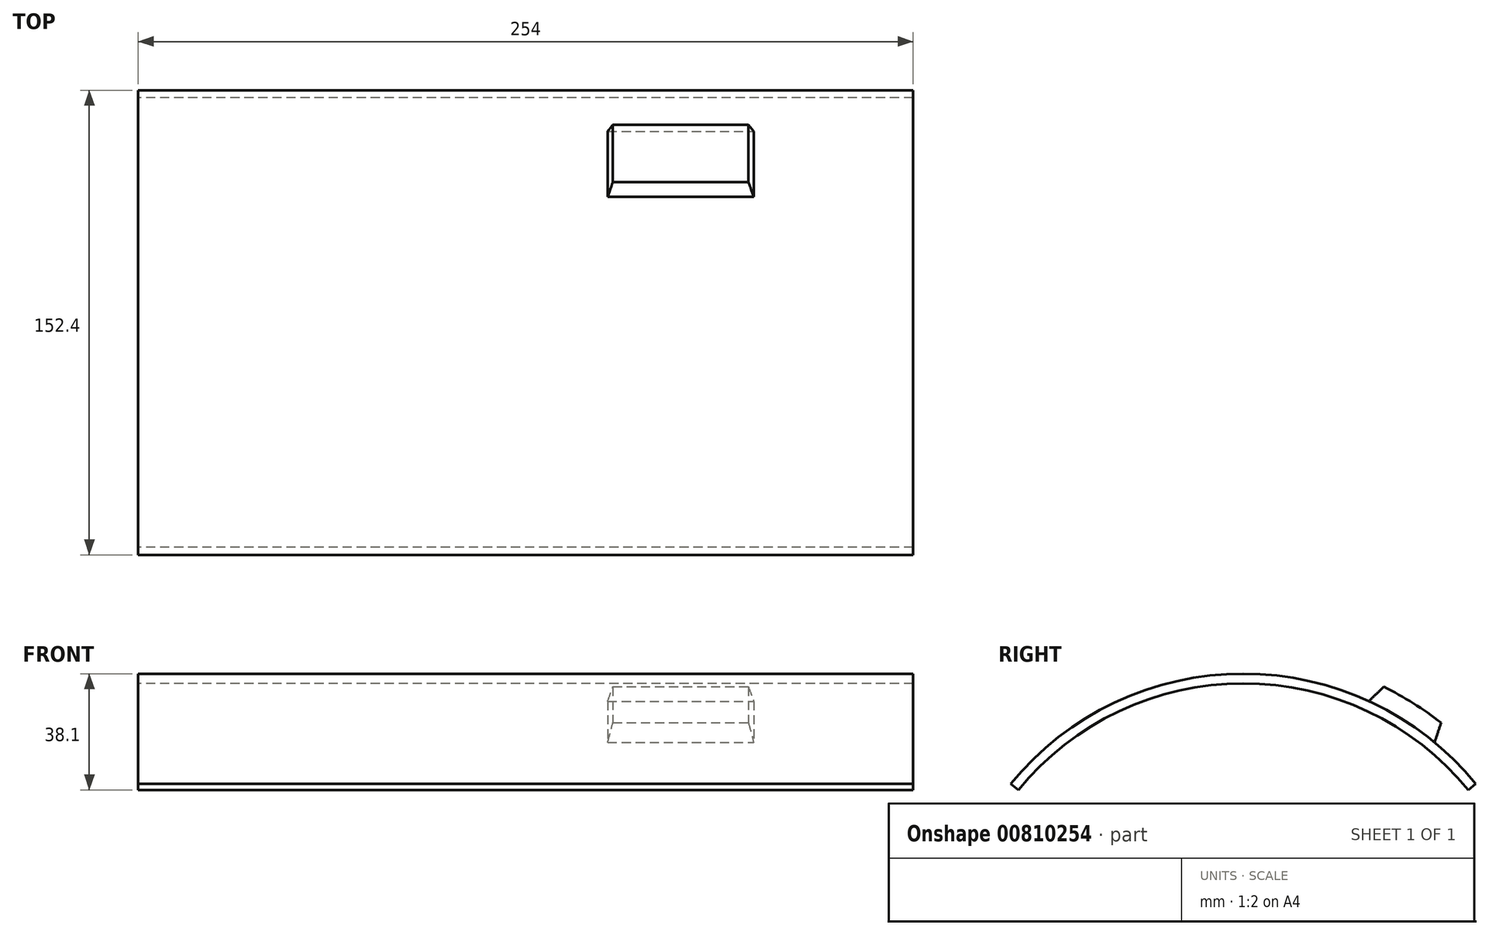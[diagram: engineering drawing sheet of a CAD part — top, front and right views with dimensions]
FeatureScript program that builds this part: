
annotation { "Feature Type Name" : "Feature", "Feature Type Description" : "" }
export const myFeature = defineFeature(function(context is Context, id is Id, definition is map)
    precondition{}
    {
        {
            var Q0;
            Q0=qCreatedBy(makeId("Right.planeOp"),FACE);
            var sketch = newSketch(context, id + "F0", { "sketchPlane" : qUnion([Q0])});
            skLineSegment(sketch, "E0", {"start": v(0, 0) * mm, "end": v(0, 53) * mm, "construction": true});
            skArc(sketch, "E1", {"start": v(73.74, 0) * mm, "mid": v(40.8, 25.75) * mm, "end": v(0, 34.93) * mm});
            skArc(sketch, "E2.0", {"start": v(76.2, 2.01) * mm, "mid": v(42.16, 28.62) * mm, "end": v(0, 38.1) * mm});
            skLineSegment(sketch, "E3", {"start": v(73.74, 0) * mm, "end": v(76.2, 2.01) * mm});
            skLineSegment(sketch, "E4.MirrorCS", {"start": v(-73.74, 0) * mm, "end": v(-76.2, 2.01) * mm});
            skArc(sketch, "E5.MirrorCS", {"start": v(-76.2, 2.01) * mm, "mid": v(-42.16, 28.62) * mm, "end": v(0, 38.1) * mm});
            skArc(sketch, "E6.MirrorCS", {"start": v(-73.74, 0) * mm, "mid": v(-40.8, 25.75) * mm, "end": v(0, 34.93) * mm});
            skLineSegment(sketch, "E7", {"start": v(0, 0) * mm, "end": v(93.37, 0) * mm, "construction": true});
            skSolve(sketch);
        }
        {
            var Q0;
            Q0 = qSketchRegion(id + "F0", true);
            extrude(context, id + "F1", {"entities" : qUnion([Q0]), "endBound" : BoundingType.SYMMETRIC, "depth" : 254 * mm, "offsetDistance" : 25.4 * mm});
        }
        {
            var Q0;
            Q0=makeQuery(id+"F1.opExtrude","SWEPT_FACE",FACE,{"disambiguationData":[OSD([sQuery(id+"F0.wireOp",EDGE,"E4.MirrorCS")])]});
            var sketch = newSketch(context, id + "F2", { "sketchPlane" : qUnion([Q0])});
            skLineSegment(sketch, "E8", {"start": v(50.8, 57.05) * mm, "end": v(50.8, 91.06) * mm, "construction": true});
            skLineSegment(sketch, "E9", {"start": v(50.8, 66.58) * mm, "end": v(73.03, 66.58) * mm});
            skLineSegment(sketch, "E10", {"start": v(73.03, 66.58) * mm, "end": v(75.58, 57.05) * mm});
            skLineSegment(sketch, "E11", {"start": v(50.8, 57.05) * mm, "end": v(75.58, 57.05) * mm});
            skLineSegment(sketch, "E12.MirrorCS", {"start": v(50.8, 66.58) * mm, "end": v(28.57, 66.58) * mm});
            skLineSegment(sketch, "E13.MirrorCS", {"start": v(28.57, 66.58) * mm, "end": v(26.02, 57.05) * mm});
            skLineSegment(sketch, "E14.MirrorCS", {"start": v(50.8, 57.05) * mm, "end": v(26.02, 57.05) * mm});
            skSolve(sketch);
        }
        {
            var Q0;
            Q0=qCreatedBy(makeId("Right.planeOp"),FACE);
            var Q1;
            Q1=sQuery(id+"F2.wireOp",VERTEX,"E10.end");
            cPlane(context, id + "F3", {"entities" : qUnion([Q0, Q1]), "cplaneType" : CPlaneType.PLANE_POINT, "offset" : 25.4 * mm, "width" : 152.4 * mm, "height" : 152.4 * mm});
        }
        {
            var Q0;
            Q0=qCreatedBy(id+"F3.planeOp",FACE);
            var sketch = newSketch(context, id + "F4", { "sketchPlane" : qUnion([Q0])});
            skArc(sketch, "E15.0", {"start": v(-76.2, 2.01) * mm, "mid": v(0, 38.1) * mm, "end": v(76.2, 2.01) * mm});
            skSolve(sketch);
        }
        {
            var Q0;
            Q0=makeQuery(id+"F2.imprint","IMPRINT",FACE,{"disambiguationData":[TD([[makeQuery(id+"F2.imprint","IMPRINT",EDGE,{"derivedFrom":sQuery(id+"F2.wireOp",EDGE,"E9")}),-1.0]])]});
            var Q1;
            Q1=sQuery(id+"F4.wireOp",EDGE,"E15.0");
            sweep(context, id + "F5", {"profiles" : qUnion([Q0]), "path" : qUnion([Q1])});
        }
        {
            var Q0;
            Q0=qCreatedBy(id+"F3.planeOp",FACE);
            var sketch = newSketch(context, id + "F6", { "sketchPlane" : qUnion([Q0])});
            skLineSegment(sketch, "E16", {"start": v(0, 0) * mm, "end": v(0, 54.2) * mm, "construction": true});
            skLineSegment(sketch, "E17", {"start": v(64.85, 21.99) * mm, "end": v(62.7, 15.57) * mm});
            skLineSegment(sketch, "E18", {"start": v(55.75, 28.4) * mm, "end": v(52.37, 23.02) * mm, "construction": true});
            skLineSegment(sketch, "E19.MirrorCS", {"start": v(46.02, 33.8) * mm, "end": v(41.18, 29.08) * mm});
            skLineSegment(sketch, "E20", {"start": v(76.2, 2.01) * mm, "end": v(81.11, 6.03) * mm});
            skArc(sketch, "E21.0", {"start": v(-81.11, 6.03) * mm, "mid": v(-22.37, 42.03) * mm, "end": v(46.02, 33.8) * mm});
            skArc(sketch, "E21.1", {"start": v(-76.2, 2.01) * mm, "mid": v(-22.13, 35.58) * mm, "end": v(41.18, 29.08) * mm});
            skArc(sketch, "E22.trimOffspring", {"start": v(64.85, 21.99) * mm, "mid": v(73.41, 14.46) * mm, "end": v(81.11, 6.03) * mm});
            skArc(sketch, "E23.trimOffspring", {"start": v(62.7, 15.57) * mm, "mid": v(69.78, 9.12) * mm, "end": v(76.2, 2.01) * mm});
            skLineSegment(sketch, "E24", {"start": v(-81.11, 6.03) * mm, "end": v(-76.2, 2.01) * mm});
            skSolve(sketch);
        }
        {
            var Q0;
            Q0 = qSketchRegion(id + "F6", true);
            extrude(context, id + "F7", {"entities" : qUnion([Q0]), "operationType" : NewBodyOperationType.REMOVE, "endBound" : BoundingType.THROUGH_ALL, "oppositeDirection" : true, "depth" : 25.4 * mm, "offsetDistance" : 25.4 * mm});
        }
    });
